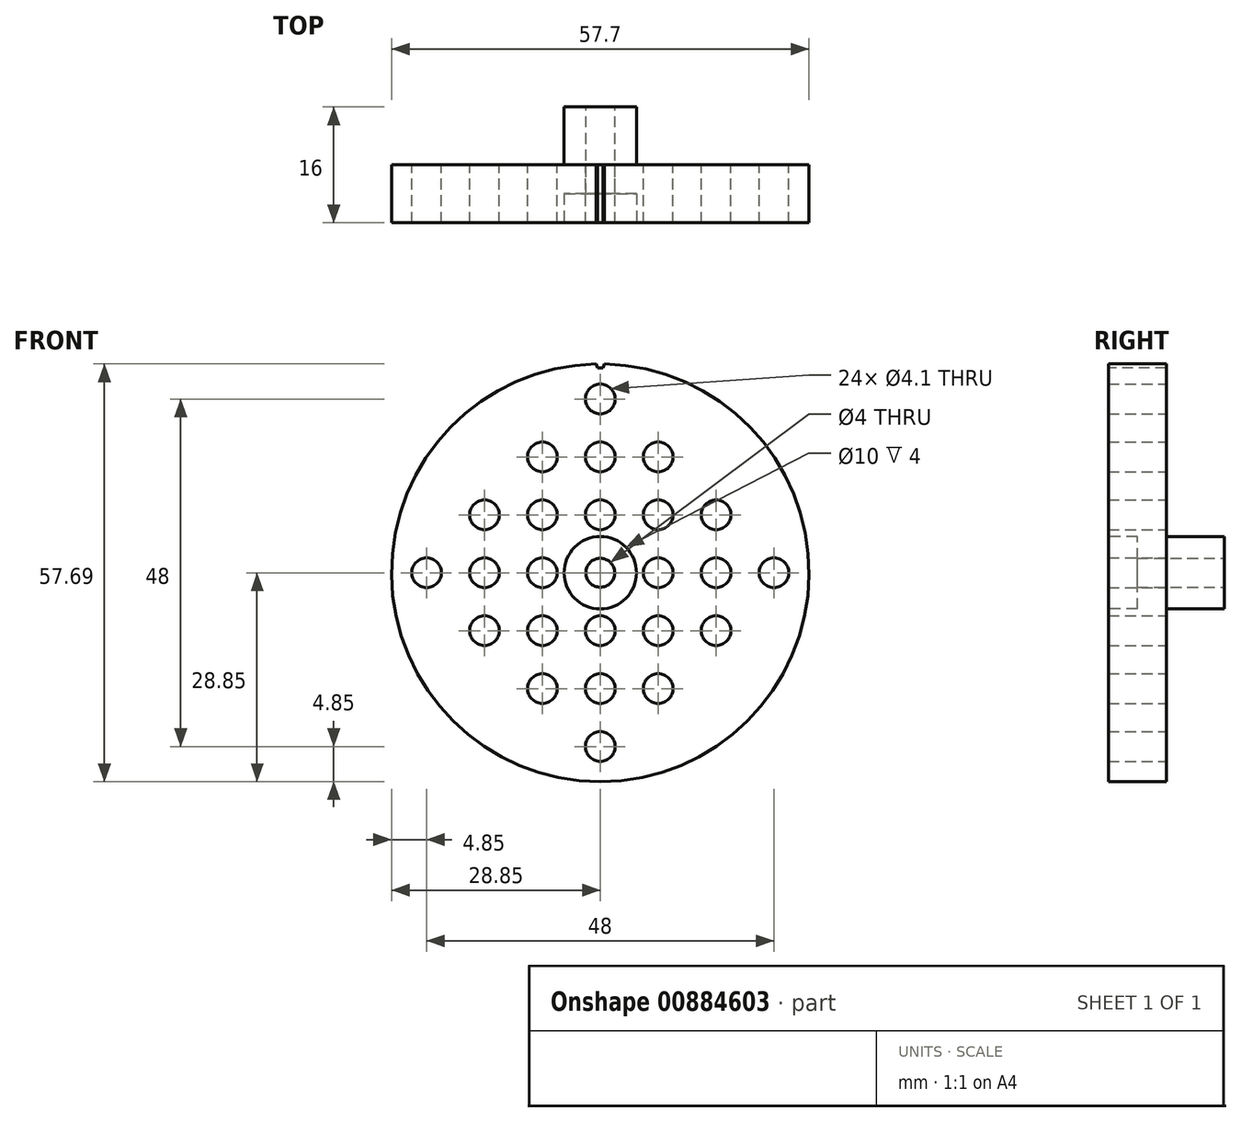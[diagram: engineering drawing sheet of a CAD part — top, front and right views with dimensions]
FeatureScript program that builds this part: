
annotation { "Feature Type Name" : "Feature", "Feature Type Description" : "" }
export const myFeature = defineFeature(function(context is Context, id is Id, definition is map)
    precondition{}
    {
        {
            var Q0;
            Q0=qCreatedBy(makeId("Front.planeOp"),FACE);
            var sketch = newSketch(context, id + "F0", { "sketchPlane" : qUnion([Q0])});
            skCircle(sketch, "E0", {"center": v(0, 0) * mm, "radius": 28.85 * mm});
            skCircle(sketch, "E1", {"center": v(-16, 0) * mm, "radius": 2.05 * mm});
            skCircle(sketch, "E2", {"center": v(-8, 0) * mm, "radius": 2.05 * mm});
            skCircle(sketch, "E3", {"center": v(-8, 8) * mm, "radius": 2.05 * mm});
            skCircle(sketch, "E4", {"center": v(0, 16) * mm, "radius": 2.05 * mm});
            skCircle(sketch, "E5", {"center": v(0, 8) * mm, "radius": 2.05 * mm});
            skCircle(sketch, "E6.MirrorC", {"center": v(8, 0) * mm, "radius": 2.05 * mm});
            skCircle(sketch, "E7.MirrorC", {"center": v(8, 8) * mm, "radius": 2.05 * mm});
            skCircle(sketch, "E8.MirrorC", {"center": v(16, 0) * mm, "radius": 2.05 * mm});
            skCircle(sketch, "E9.MirrorC", {"center": v(-8, -8) * mm, "radius": 2.05 * mm});
            skCircle(sketch, "E10.MirrorC", {"center": v(0, -8) * mm, "radius": 2.05 * mm});
            skCircle(sketch, "E11.MirrorC", {"center": v(8, -8) * mm, "radius": 2.05 * mm});
            skCircle(sketch, "E12.MirrorC", {"center": v(0, -16) * mm, "radius": 2.05 * mm});
            skCircle(sketch, "E13", {"center": v(0, 0) * mm, "radius": 2 * mm});
            skCircle(sketch, "E14", {"center": v(0, 24) * mm, "radius": 2.05 * mm});
            skCircle(sketch, "E15", {"center": v(8, 16) * mm, "radius": 2.05 * mm});
            skCircle(sketch, "E16", {"center": v(16, 8) * mm, "radius": 2.05 * mm});
            skCircle(sketch, "E17", {"center": v(24, 0) * mm, "radius": 2.05 * mm});
            skCircle(sketch, "E18.MirrorC", {"center": v(16, -8) * mm, "radius": 2.05 * mm});
            skCircle(sketch, "E19.MirrorC", {"center": v(8, -16) * mm, "radius": 2.05 * mm});
            skCircle(sketch, "E20.MirrorC", {"center": v(0, -24) * mm, "radius": 2.05 * mm});
            skCircle(sketch, "E21.MirrorC", {"center": v(-8, -16) * mm, "radius": 2.05 * mm});
            skCircle(sketch, "E22.MirrorC", {"center": v(-16, -8) * mm, "radius": 2.05 * mm});
            skCircle(sketch, "E23.MirrorC", {"center": v(-24, 0) * mm, "radius": 2.05 * mm});
            skCircle(sketch, "E24.MirrorC", {"center": v(-16, 8) * mm, "radius": 2.05 * mm});
            skCircle(sketch, "E25.MirrorC", {"center": v(-8, 16) * mm, "radius": 2.05 * mm});
            skSolve(sketch);
        }
        {
            var Q0;
            Q0=makeQuery(id+"F0.imprint","IMPRINT",FACE,{"disambiguationData":[TD([[makeQuery(id+"F0.imprint","IMPRINT",EDGE,{"derivedFrom":sQuery(id+"F0.wireOp",EDGE,"E0")}),1.0]])]});
            extrude(context, id + "F1", {"entities" : qUnion([Q0]), "endBound" : BoundingType.SYMMETRIC, "depth" : 8 * mm, "offsetDistance" : 25.4 * mm});
        }
        {
            var Q0;
            Q0=makeQuery(id+"F1.opExtrude","CAP_FACE",FACE,{"disambiguationData":[OSD([sQuery(id+"F0.wireOp",EDGE,"E0"),sQuery(id+"F0.wireOp",EDGE,"E1"),sQuery(id+"F0.wireOp",EDGE,"E2"),sQuery(id+"F0.wireOp",EDGE,"E3"),sQuery(id+"F0.wireOp",EDGE,"E4"),sQuery(id+"F0.wireOp",EDGE,"E5"),sQuery(id+"F0.wireOp",EDGE,"E6.MirrorC"),sQuery(id+"F0.wireOp",EDGE,"E7.MirrorC"),sQuery(id+"F0.wireOp",EDGE,"E8.MirrorC"),sQuery(id+"F0.wireOp",EDGE,"E9.MirrorC"),sQuery(id+"F0.wireOp",EDGE,"E10.MirrorC"),sQuery(id+"F0.wireOp",EDGE,"E11.MirrorC"),sQuery(id+"F0.wireOp",EDGE,"E12.MirrorC"),sQuery(id+"F0.wireOp",EDGE,"E13")])],"isStart":false});
            var sketch = newSketch(context, id + "F2", { "sketchPlane" : qUnion([Q0])});
            skCircle(sketch, "E26", {"center": v(0, 0) * mm, "radius": 5 * mm});
            skSolve(sketch);
        }
        {
            var Q0;
            Q0=qSketchRegion(id+"F2",true);
            extrude(context, id + "F3", {"entities" : qUnion([Q0]), "operationType" : NewBodyOperationType.REMOVE, "oppositeDirection" : true, "depth" : 4 * mm, "offsetDistance" : 25.4 * mm});
        }
        {
            var Q0;
            Q0=makeQuery(id+"F1.opExtrude","CAP_FACE",FACE,{"disambiguationData":[OSD([sQuery(id+"F0.wireOp",EDGE,"E0"),sQuery(id+"F0.wireOp",EDGE,"E1"),sQuery(id+"F0.wireOp",EDGE,"E2"),sQuery(id+"F0.wireOp",EDGE,"E3"),sQuery(id+"F0.wireOp",EDGE,"E4"),sQuery(id+"F0.wireOp",EDGE,"E5"),sQuery(id+"F0.wireOp",EDGE,"E6.MirrorC"),sQuery(id+"F0.wireOp",EDGE,"E7.MirrorC"),sQuery(id+"F0.wireOp",EDGE,"E8.MirrorC"),sQuery(id+"F0.wireOp",EDGE,"E9.MirrorC"),sQuery(id+"F0.wireOp",EDGE,"E10.MirrorC"),sQuery(id+"F0.wireOp",EDGE,"E11.MirrorC"),sQuery(id+"F0.wireOp",EDGE,"E12.MirrorC"),sQuery(id+"F0.wireOp",EDGE,"E13")])],"isStart":false});
            var sketch = newSketch(context, id + "F4", { "sketchPlane" : qUnion([Q0])});
            skLineSegment(sketch, "E27", {"start": v(-1.08, 30.84) * mm, "end": v(-0.4, 28.3) * mm});
            skLineSegment(sketch, "E28", {"start": v(0.4, 28.3) * mm, "end": v(1.08, 30.84) * mm});
            skLineSegment(sketch, "E29", {"start": v(1.08, 30.84) * mm, "end": v(-1.08, 30.84) * mm});
            skArc(sketch, "E30", {"start": v(0.4, 28.3) * mm, "mid": v(0, 28.3) * mm, "end": v(-0.4, 28.3) * mm});
            skSolve(sketch);
        }
        {
            var Q0;
            Q0=qSketchRegion(id+"F4",true);
            extrude(context, id + "F5", {"entities" : qUnion([Q0]), "operationType" : NewBodyOperationType.REMOVE, "oppositeDirection" : true, "depth" : 25.4 * mm, "offsetDistance" : 25.4 * mm});
        }
        {
            var Q0;
            Q0=makeQuery(id+"F1.opExtrude","CAP_FACE",FACE,{"disambiguationData":[OSD([sQuery(id+"F0.wireOp",EDGE,"E0"),sQuery(id+"F0.wireOp",EDGE,"E1"),sQuery(id+"F0.wireOp",EDGE,"E2"),sQuery(id+"F0.wireOp",EDGE,"E3"),sQuery(id+"F0.wireOp",EDGE,"E4"),sQuery(id+"F0.wireOp",EDGE,"E5"),sQuery(id+"F0.wireOp",EDGE,"E6.MirrorC"),sQuery(id+"F0.wireOp",EDGE,"E7.MirrorC"),sQuery(id+"F0.wireOp",EDGE,"E8.MirrorC"),sQuery(id+"F0.wireOp",EDGE,"E9.MirrorC"),sQuery(id+"F0.wireOp",EDGE,"E10.MirrorC"),sQuery(id+"F0.wireOp",EDGE,"E11.MirrorC"),sQuery(id+"F0.wireOp",EDGE,"E12.MirrorC"),sQuery(id+"F0.wireOp",EDGE,"E13")])],"isStart":true});
            var sketch = newSketch(context, id + "F6", { "sketchPlane" : qUnion([Q0])});
            skCircle(sketch, "E31", {"center": v(0, 0) * mm, "radius": 5 * mm});
            skCircle(sketch, "E32", {"center": v(0, 0) * mm, "radius": 2 * mm});
            skSolve(sketch);
        }
        {
            var Q0;
            Q0=qSketchRegion(id+"F6",true);
            extrude(context, id + "F7", {"entities" : qUnion([Q0]), "operationType" : NewBodyOperationType.ADD, "depth" : 8 * mm, "offsetDistance" : 25.4 * mm});
        }
    });
